# Revit family: Deca_Bidê com 3 furos_Axis_B.47
name_source: partatom
category: Plumbing Fixtures
units: mm (PartAtom-declared; Revit-internal decimal feet)

## family parameters
Cut with Voids When Loaded = No
Host = Face
Part Type = Normal
Room Calculation Point = No
Round Connector Dimension = Use Radius
Shared = No

## types (2) — shared parameters
Acompanha o Produto = -
Aprovado por = quattroD
Atendimento ao Cliente = 0800-0117073
Categoria = BACIAS E BIDES
Composição Anel Vedação = -
Composição Assento = -
Composição Básica = Argila, feldspato, caulim, vidrados e corantes inorgânicos.
Composição Componente = Não Possui
Consumo = -
Cor Interna = -
Cor Secundária = -
Cores Componente = Não Possui
Criado por = quattroD
Código Pai = B.47
Description = Bidê com 3 furos
Diâmetro Ponto de Esgoto = 0.04 m
Diâmetro Água Fria = 0.02 m
Diâmetro Água Quente = 0.02 m
Informações Complementares = -
Itens de Instalação = 1895.C14; 1895.C26; 1895.C33; 1895.C34; 1895.C35; 1895.C37; 1895.C38; 1895.C40.CR; 1895.C43; 1895.C50; 1895.C52; 1895.C64; 1895.C81; 1895.C84; 1895.C86; 1895.C87; 1895.C90; 1895.C94; SP.121.01
Linha = Axis
Manufacturer = Deca
Norma = NBR-16728-1;NBR-16728-2
Peso Líquido (Kg) = 26.771
Pressão máx. funcionamento = -
Pressão mín. Aquec. Acúmulo = -
Pressão mín. Aquec. Passagem = -
Pressão mín. funcionamento = -
Raio Ponto de Esgoto = 0.02 m
Raio Água Fria = 0.01 m
Raio Água Quente = 0.01 m
Saída de Esgoto = Saída de Esgoto Vertical
Segmento = Banheiro Médio
Tipo de dispositivo economizador = -
Tipo de mecanismo utilizado = -
Tipo de rosca de entrada = -
Tipo de rosca de saída = -
URL = www.deca.com.br
Vazão na Pressão máx. (L/min) = -
Vazão na Pressão mín. (L/min) = -
zero-valued in all types: Default Elevation

## per-type parameters (varying)
| type | Cor Principal | Material | Model |
| B.47.17_Branco | Branco | Deca_Branco | B.47.17 |
| B.47.95_Ébano | Ébano | Deca_Ébano | B.47.95 |

## geometry (parser evidence)
native form markers: Sweep x2
no freeform markers — native parametric forms only
